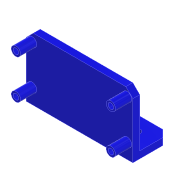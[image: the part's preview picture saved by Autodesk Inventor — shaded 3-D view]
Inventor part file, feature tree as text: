
AUTODESK INVENTOR PART (.ipt)
format: ipt  version: 2022 (Build 260153000, 153)  size: 189,440 bytes
history: native  units: mm
features: sketch x5, extrude x3, hole x2, projected_geometry x2, chamfer x1
ambient origin geometry x8: Origin, YZ Plane, XZ Plane, XY Plane, X Axis, Y Axis, Z Axis, Center Point
bodies: Solid1 (feature_tree)
feature tree (13):
  extrude  "Extrusion1"  Depth=44.0mm
  extrude  "Extrusion2"  Depth=3.0mm TaperAngle=0.0deg
  hole  "Hole1"  [1 undecoded]
  hole  "Hole2"  [1 undecoded]
  chamfer  "Chamfer2"  Distance=3.0mm Angle=45.0deg
  extrude  "Extrusion3"  Depth=2.0mm
  sketch  "Sketch1"  dims[d0=20.0mm d1=44.0mm]
  sketch  "Sketch2"  dims[d2=2.0mm d3=3.0mm d4=0.0mm]
  sketch  "Sketch3"  dims[d6=3.0mm d7=0.0mm d8=2.0mm]
  sketch  "Sketch5"  dims[d9=2.0mm d10=2.0mm]
  sketch  "Sketch6"  dims[d11=2.0mm d14=2.4mm d15=6.0mm d16=4.0mm d17=2.0mm d18=90.0deg d19=6.0mm d20=0.0mm d33=3.4mm d34=6.0mm d35=4.0mm d36=2.0mm d37=90.0deg d38=6.0mm d39=0.0mm d40=3.0mm d41=2.0mm d42=45.0deg d43=0.5mm d44=44.0mm d45=20.0mm d46=4.0mm d47=4.0mm d49=4.0mm d50=4.0mm d51=7.0mm d52=0.0mm d54=46.0mm d55=16.0mm d56=13.0mm d57=6.5mm d58=30.0mm d59=46.0mm d60=2.0mm d61=1.0mm d62=1.0mm]
  projected_geometry  "Project Cut Edges2"
  projected_geometry  "Project Cut Edges3"
note: 2 required parameter values undecoded (feature->parameter linkage not recoverable at this tier; creation-order binding heuristic only, values carry confidence <= 0.55)
